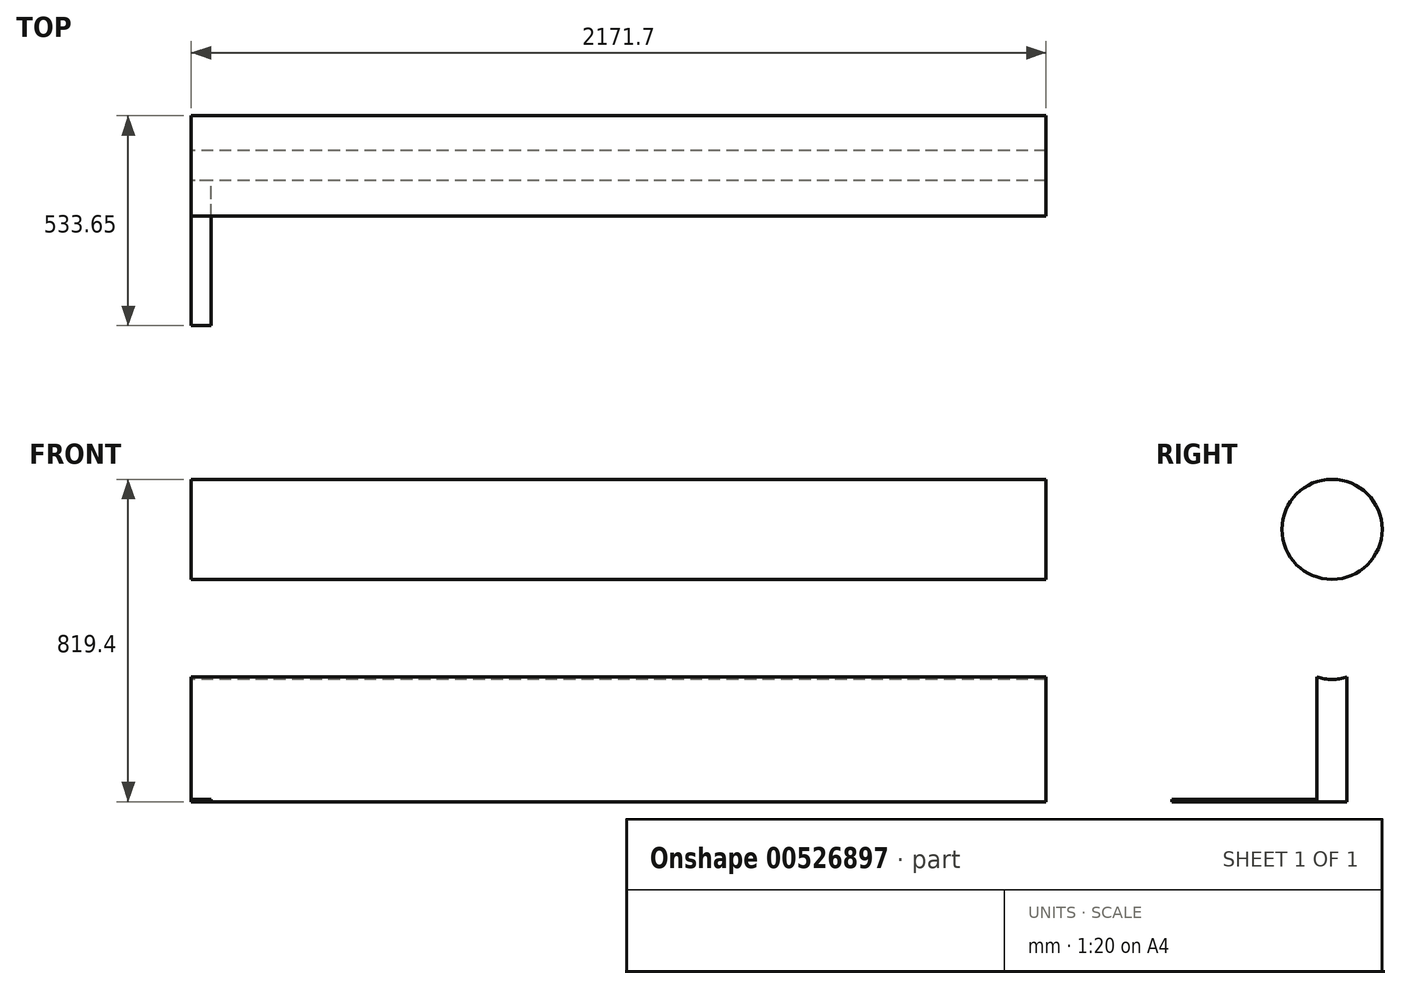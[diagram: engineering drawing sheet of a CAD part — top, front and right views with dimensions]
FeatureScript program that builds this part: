
annotation { "Feature Type Name" : "Feature", "Feature Type Description" : "" }
export const myFeature = defineFeature(function(context is Context, id is Id, definition is map)
    precondition{}
    {
        {
            var Q0;
            Q0=qCreatedBy(makeId("Right.planeOp"),FACE);
            var sketch = newSketch(context, id + "F0", { "sketchPlane" : qUnion([Q0])});
            skLineSegment(sketch, "E0", {"start": v(38.1, 0) * mm, "end": v(0, 0) * mm});
            skLineSegment(sketch, "E1.MirrorCS", {"start": v(38.1, 1422.4) * mm, "end": v(0, 1422.4) * mm});
            skLineSegment(sketch, "E2.MirrorCS", {"start": v(-38.1, 0) * mm, "end": v(0, 0) * mm});
            skLineSegment(sketch, "E3", {"start": v(0, 0) * mm, "end": v(0, 564.9) * mm});
            skLineSegment(sketch, "E4", {"start": v(0, 0) * mm, "end": v(0, 692.15) * mm});
            skCircle(sketch, "E5", {"center": v(0, 692.15) * mm, "radius": 127.25 * mm});
            skLineSegment(sketch, "E6", {"start": v(0, 0) * mm, "end": v(0, 437.9) * mm});
            skCircle(sketch, "E7", {"center": v(0, 437.9) * mm, "radius": 127 * mm});
            skLineSegment(sketch, "E8", {"start": v(38.1, 0) * mm, "end": v(38.1, 316.75) * mm});
            skLineSegment(sketch, "E9", {"start": v(-38.1, 0) * mm, "end": v(-38.1, 316.75) * mm});
            skSolve(sketch);
        }
        {
            var Q0;
            Q0=makeQuery(id+"F0.imprint","IMPRINT",FACE,{"disambiguationData":[TD([[makeQuery(id+"F0.imprint","IMPRINT",EDGE,{"derivedFrom":sQuery(id+"F0.wireOp",EDGE,"E5")}),1.0]])]});
            var Q1;
            {var subQ0=sQuery(id+"F0.wireOp",EDGE,"E6");var subQ1=sQuery(id+"F0.wireOp",EDGE,"E4");var subQ2=makeQuery(id+"F0.imprint","INTERSECT",VERTEX,{"derivedFrom":[subQ1,subQ0]});Q1=makeQuery(id+"F0.imprint","IMPRINT",FACE,{"disambiguationData":[TD([[makeQuery(id+"F0.imprint","IMPRINT",EDGE,{"disambiguationData":[TD([[subQ2,1.0]])],"derivedFrom":subQ0}),-1.0]])]});}
            var Q2;
            {var subQ0=sQuery(id+"F0.wireOp",EDGE,"E6");var subQ1=sQuery(id+"F0.wireOp",EDGE,"E4");var subQ2=makeQuery(id+"F0.imprint","INTERSECT",VERTEX,{"derivedFrom":[subQ1,subQ0]});Q2=makeQuery(id+"F0.imprint","IMPRINT",FACE,{"disambiguationData":[TD([[makeQuery(id+"F0.imprint","IMPRINT",EDGE,{"disambiguationData":[TD([[subQ2,1.0]])],"derivedFrom":subQ0}),1.0]])]});}
            var Q3;
            {var subQ0=sQuery(id+"F0.wireOp",EDGE,"E0");Q3=makeQuery(id+"F0.imprint","IMPRINT",FACE,{"disambiguationData":[TD([[makeQuery(id+"F0.imprint","IMPRINT",EDGE,{"derivedFrom":subQ0}),-1.0]])]});}
            var Q4;
            {var subQ0=sQuery(id+"F0.wireOp",EDGE,"E2.MirrorCS");Q4=makeQuery(id+"F0.imprint","IMPRINT",FACE,{"disambiguationData":[TD([[makeQuery(id+"F0.imprint","IMPRINT",EDGE,{"derivedFrom":subQ0}),1.0]])]});}
            extrude(context, id + "F1", {"entities" : qUnion([Q0, Q1, Q2, Q3, Q4]), "depth" : 2171.7 * mm, "offsetDistance" : 25.4 * mm});
        }
        {
            var Q0;
            Q0=qCreatedBy(makeId("Front.planeOp"),FACE);
            var sketch = newSketch(context, id + "F2", { "sketchPlane" : qUnion([Q0])});
            skLineSegment(sketch, "E10.bottom", {"start": v(0, 0) * mm, "end": v(50.8, 0) * mm});
            skLineSegment(sketch, "E10.top", {"start": v(0, 6.35) * mm, "end": v(50.8, 6.35) * mm});
            skLineSegment(sketch, "E10.left", {"start": v(0, 0) * mm, "end": v(0, 6.35) * mm});
            skLineSegment(sketch, "E10.right", {"start": v(50.8, 0) * mm, "end": v(50.8, 6.35) * mm});
            skSolve(sketch);
        }
        {
            var Q0;
            Q0 = qSketchRegion(id + "F2", true);
            extrude(context, id + "F3", {"entities" : qUnion([Q0]), "operationType" : NewBodyOperationType.ADD, "depth" : 406.4 * mm, "offsetDistance" : 25.4 * mm});
        }
    });
